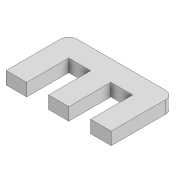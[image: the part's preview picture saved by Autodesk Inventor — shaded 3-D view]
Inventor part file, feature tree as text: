
AUTODESK INVENTOR PART (.ipt)
format: ipt  version: 2022 (Build 260153000, 153)  size: 125,952 bytes
history: native  units: mm
features: extrude x1, fillet x1, thicken_offset x1, sketch x1
ambient origin geometry x8: Origin, YZ Plane, XZ Plane, XY Plane, X Axis, Y Axis, Z Axis, Center Point
bodies: Solid1 (feature_tree)
feature tree (4):
  extrude  "Extrusion1"  Depth=3.0mm
  fillet  "Fillet1"  Radius=25.0mm
  thicken_offset  "Thicken3"
  sketch  "Sketch1"  dims[d0=3.0mm d1=3.0mm d3=25.0mm d4=2.0mm d5=8.0mm d6=6.0mm d7=5.0mm d9=3.0mm d10=9.9mm d11=5.0mm d12=10.0mm d13=5.0mm d14=5.0mm d15=5.0mm d16=5.0mm d17=3.0mm d18=0.0mm d19=5.0mm d20=2.0mm d35=0.1mm d36=0.1mm]
